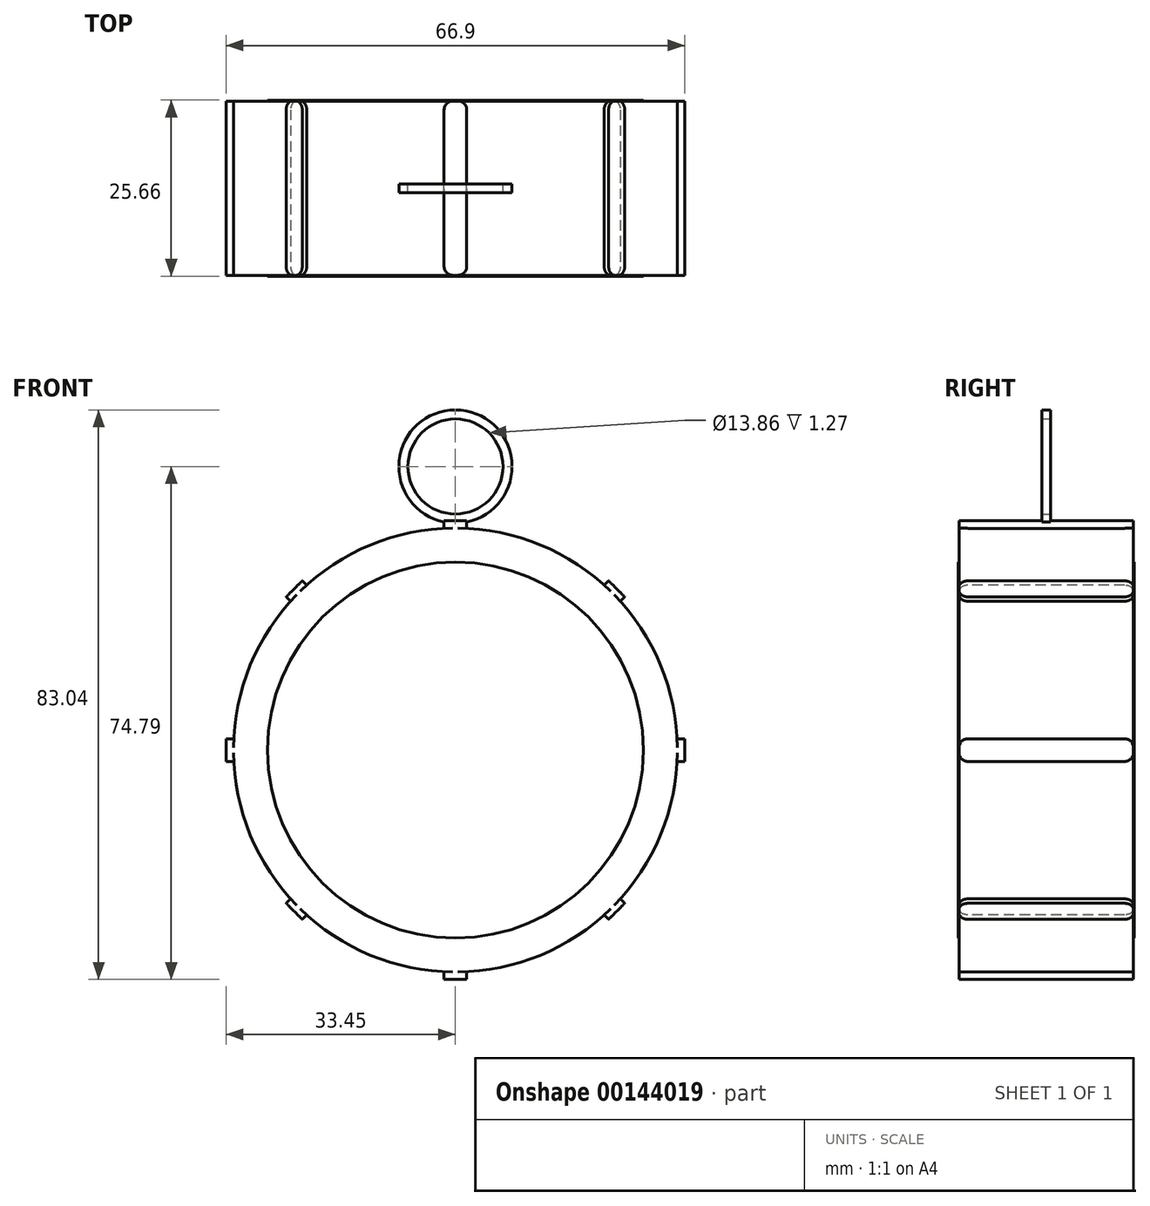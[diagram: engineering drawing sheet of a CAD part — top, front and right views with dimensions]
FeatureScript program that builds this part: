
annotation { "Feature Type Name" : "Feature", "Feature Type Description" : "" }
export const myFeature = defineFeature(function(context is Context, id is Id, definition is map)
    precondition{}
    {
        {
            var Q0;
            Q0=qCreatedBy(makeId("Front.planeOp"),FACE);
            var sketch = newSketch(context, id + "F0", { "sketchPlane" : qUnion([Q0])});
            skCircle(sketch, "E0", {"center": v(0, 0) * mm, "radius": 32.37 * mm});
            skSolve(sketch);
        }
        {
            var Q0;
            Q0 = qSketchRegion(id + "F0", true);
            extrude(context, id + "F1", {"entities" : qUnion([Q0]), "depth" : 25.4 * mm, "symmetric" : true});
        }
        {
            var Q0;
            Q0=qCreatedBy(makeId("Front.planeOp"),FACE);
            var sketch = newSketch(context, id + "F2", { "sketchPlane" : qUnion([Q0])});
            skCircle(sketch, "E1", {"center": v(0, 0) * mm, "radius": 27.4 * mm});
            skSolve(sketch);
        }
        {
            var Q0;
            Q0 = qSketchRegion(id + "F2", true);
            extrude(context, id + "F3", {"entities" : qUnion([Q0]), "operationType" : NewBodyOperationType.ADD, "depth" : 25.65 * mm, "symmetric" : true});
        }
        {
            var Q0;
            Q0=makeQuery(id+"F1.opExtrude","CAP_FACE",FACE,{"disambiguationData":[OSD([sQuery(id+"F0.wireOp",EDGE,"E0")])],"isStart":false});
            var sketch = newSketch(context, id + "F4", { "sketchPlane" : qUnion([Q0])});
            skPoint(sketch, "E2.middle", {"position": v(0, 0) * mm});
            skLineSegment(sketch, "E3", {"start": v(23.5, 23.5) * mm, "end": v(22.34, 24.68) * mm});
            skLineSegment(sketch, "E4", {"start": v(22.34, 24.68) * mm, "end": v(21.7, 24.03) * mm});
            skLineSegment(sketch, "E5", {"start": v(23.5, 23.5) * mm, "end": v(24.68, 22.34) * mm});
            skLineSegment(sketch, "E6", {"start": v(24.68, 22.34) * mm, "end": v(24.03, 21.7) * mm});
            skLineSegment(sketch, "E7.MirrorCS", {"start": v(24.68, -22.34) * mm, "end": v(24.03, -21.7) * mm});
            skLineSegment(sketch, "E8.MirrorCS", {"start": v(23.5, -23.5) * mm, "end": v(24.68, -22.34) * mm});
            skLineSegment(sketch, "E9.MirrorCS", {"start": v(23.5, -23.5) * mm, "end": v(22.34, -24.68) * mm});
            skLineSegment(sketch, "E10.MirrorCS", {"start": v(22.34, -24.68) * mm, "end": v(21.7, -24.03) * mm});
            skLineSegment(sketch, "E11.MirrorCS", {"start": v(-22.34, 24.68) * mm, "end": v(-21.7, 24.03) * mm});
            skLineSegment(sketch, "E12.MirrorCS", {"start": v(-23.5, 23.5) * mm, "end": v(-22.34, 24.68) * mm});
            skLineSegment(sketch, "E13.MirrorCS", {"start": v(-23.5, 23.5) * mm, "end": v(-24.68, 22.34) * mm});
            skLineSegment(sketch, "E14.MirrorCS", {"start": v(-24.68, 22.34) * mm, "end": v(-24.03, 21.7) * mm});
            skLineSegment(sketch, "E15.MirrorCS", {"start": v(-23.5, -23.5) * mm, "end": v(-24.68, -22.34) * mm});
            skLineSegment(sketch, "E16.MirrorCS", {"start": v(-24.68, -22.34) * mm, "end": v(-24.03, -21.7) * mm});
            skLineSegment(sketch, "E17.MirrorCS", {"start": v(-23.5, -23.5) * mm, "end": v(-22.34, -24.68) * mm});
            skLineSegment(sketch, "E18.MirrorCS", {"start": v(-22.34, -24.68) * mm, "end": v(-21.7, -24.03) * mm});
            skLineSegment(sketch, "E19", {"start": v(0, 33.45) * mm, "end": v(-1.65, 33.45) * mm});
            skLineSegment(sketch, "E20", {"start": v(-1.65, 33.45) * mm, "end": v(-1.65, 32.33) * mm});
            skLineSegment(sketch, "E21", {"start": v(0, 33.45) * mm, "end": v(1.65, 33.45) * mm});
            skLineSegment(sketch, "E22", {"start": v(1.65, 33.45) * mm, "end": v(1.65, 32.33) * mm});
            skLineSegment(sketch, "E23.MirrorCS", {"start": v(0, -33.45) * mm, "end": v(-1.65, -33.45) * mm});
            skLineSegment(sketch, "E24.MirrorCS", {"start": v(-1.65, -33.45) * mm, "end": v(-1.65, -32.33) * mm});
            skLineSegment(sketch, "E25.MirrorCS", {"start": v(0, -33.45) * mm, "end": v(1.65, -33.45) * mm});
            skLineSegment(sketch, "E26.MirrorCS", {"start": v(1.65, -33.45) * mm, "end": v(1.65, -32.33) * mm});
            skLineSegment(sketch, "E27", {"start": v(-33.45, 0) * mm, "end": v(-33.45, 1.65) * mm});
            skLineSegment(sketch, "E28", {"start": v(-33.45, 1.65) * mm, "end": v(-32.33, 1.65) * mm});
            skLineSegment(sketch, "E29", {"start": v(-33.45, 0) * mm, "end": v(-33.45, -1.65) * mm});
            skLineSegment(sketch, "E30", {"start": v(-33.45, -1.65) * mm, "end": v(-32.33, -1.65) * mm});
            skLineSegment(sketch, "E31.MirrorCS", {"start": v(33.45, 1.65) * mm, "end": v(32.33, 1.65) * mm});
            skLineSegment(sketch, "E32.MirrorCS", {"start": v(33.45, 0) * mm, "end": v(33.45, 1.65) * mm});
            skLineSegment(sketch, "E33.MirrorCS", {"start": v(33.45, 0) * mm, "end": v(33.45, -1.65) * mm});
            skLineSegment(sketch, "E34.MirrorCS", {"start": v(33.45, -1.65) * mm, "end": v(32.33, -1.65) * mm});
            skSolve(sketch);
        }
        {
            var Q0;
            {var subQ1=sQuery(id+"F4.wireOp",EDGE,"E11.MirrorCS");Q0=makeQuery(id+"F4.imprint","IMPRINT",FACE,{"disambiguationData":[TD([[makeQuery(id+"F4.imprint","IMPRINT",EDGE,{"derivedFrom":subQ1}),-1.0]])]});}
            var Q1;
            Q1=makeQuery(id+"F4.imprint","IMPRINT",FACE,{"disambiguationData":[TD([[makeQuery(id+"F4.imprint","IMPRINT",EDGE,{"derivedFrom":sQuery(id+"F4.wireOp",EDGE,"E3")}),1.0]])]});
            var Q2;
            {var subQ1=sQuery(id+"F4.wireOp",EDGE,"E7.MirrorCS");Q2=makeQuery(id+"F4.imprint","IMPRINT",FACE,{"disambiguationData":[TD([[makeQuery(id+"F4.imprint","IMPRINT",EDGE,{"derivedFrom":subQ1}),1.0]])]});}
            var Q3;
            Q3=makeQuery(id+"F4.imprint","IMPRINT",FACE,{"disambiguationData":[TD([[makeQuery(id+"F4.imprint","IMPRINT",EDGE,{"derivedFrom":sQuery(id+"F4.wireOp",EDGE,"E15.MirrorCS")}),-1.0]])]});
            var Q4;
            Q4=makeQuery(id+"F4.imprint","IMPRINT",FACE,{"disambiguationData":[TD([[makeQuery(id+"F4.imprint","IMPRINT",EDGE,{"derivedFrom":sQuery(id+"F4.wireOp",EDGE,"E23.MirrorCS")}),-1.0]])]});
            var Q5;
            Q5=makeQuery(id+"F4.imprint","IMPRINT",FACE,{"disambiguationData":[TD([[makeQuery(id+"F4.imprint","IMPRINT",EDGE,{"derivedFrom":sQuery(id+"F4.wireOp",EDGE,"E27")}),-1.0]])]});
            var Q6;
            {var subQ1=sQuery(id+"F4.wireOp",EDGE,"E31.MirrorCS");Q6=makeQuery(id+"F4.imprint","IMPRINT",FACE,{"disambiguationData":[TD([[makeQuery(id+"F4.imprint","IMPRINT",EDGE,{"derivedFrom":subQ1}),1.0]])]});}
            var Q7;
            Q7=makeQuery(id+"F4.imprint","IMPRINT",FACE,{"disambiguationData":[TD([[makeQuery(id+"F4.imprint","IMPRINT",EDGE,{"derivedFrom":sQuery(id+"F4.wireOp",EDGE,"E19")}),1.0]])]});
            extrude(context, id + "F5", {"entities" : qUnion([Q0, Q1, Q2, Q3, Q4, Q5, Q6, Q7]), "operationType" : NewBodyOperationType.ADD, "oppositeDirection" : true, "depth" : 25.4 * mm});
        }
        {
            var Q0;
            Q0=makeQuery(id+"Fw6DQcA7fibf5eo_1.opExtrude","SWEPT_EDGE",EDGE,{"disambiguationData":[OSD([sQuery(id+"FSgP6cTA9YGb6rM_1.wireOp",EDGE,"k7nYMJ6Q-pWd2-LHft-FCDd-KbcVLsTTeNov.top"),sQuery(id+"FSgP6cTA9YGb6rM_1.wireOp",EDGE,"k7nYMJ6Q-pWd2-LHft-FCDd-KbcVLsTTeNov.left")])]});
            var Q1;
            Q1=makeQuery(id+"Fw6DQcA7fibf5eo_1.opExtrude","SWEPT_EDGE",EDGE,{"disambiguationData":[OSD([sQuery(id+"FSgP6cTA9YGb6rM_1.wireOp",EDGE,"k7nYMJ6Q-pWd2-LHft-FCDd-KbcVLsTTeNov.bottom"),sQuery(id+"FSgP6cTA9YGb6rM_1.wireOp",EDGE,"k7nYMJ6Q-pWd2-LHft-FCDd-KbcVLsTTeNov.left")])]});
            var Q2;
            Q2=makeQuery(id+"Fw6DQcA7fibf5eo_1.opExtrude","SWEPT_EDGE",EDGE,{"disambiguationData":[OSD([sQuery(id+"FSgP6cTA9YGb6rM_1.wireOp",EDGE,"k7nYMJ6Q-pWd2-LHft-FCDd-KbcVLsTTeNov.top"),sQuery(id+"FSgP6cTA9YGb6rM_1.wireOp",EDGE,"k7nYMJ6Q-pWd2-LHft-FCDd-KbcVLsTTeNov.right")])]});
            var Q3;
            Q3=makeQuery(id+"Fw6DQcA7fibf5eo_1.opExtrude","SWEPT_EDGE",EDGE,{"disambiguationData":[OSD([sQuery(id+"FSgP6cTA9YGb6rM_1.wireOp",EDGE,"k7nYMJ6Q-pWd2-LHft-FCDd-KbcVLsTTeNov.bottom"),sQuery(id+"FSgP6cTA9YGb6rM_1.wireOp",EDGE,"k7nYMJ6Q-pWd2-LHft-FCDd-KbcVLsTTeNov.right")])]});
            var Q4;
            Q4=makeQuery(id+"F5.opExtrude","CAP_EDGE",EDGE,{"disambiguationData":[OSD([sQuery(id+"F4.wireOp",EDGE,"E7.MirrorCS")])],"isStart":false});
            var Q5;
            Q5=makeQuery(id+"F5.opExtrude","CAP_EDGE",EDGE,{"disambiguationData":[OSD([sQuery(id+"F4.wireOp",EDGE,"E10.MirrorCS")])],"isStart":false});
            var Q6;
            Q6=makeQuery(id+"F5.opExtrude","CAP_EDGE",EDGE,{"disambiguationData":[OSD([sQuery(id+"F4.wireOp",EDGE,"E7.MirrorCS")])],"isStart":true});
            var Q7;
            Q7=makeQuery(id+"F5.opExtrude","CAP_EDGE",EDGE,{"disambiguationData":[OSD([sQuery(id+"F4.wireOp",EDGE,"E10.MirrorCS")])],"isStart":true});
            var Q8;
            Q8=makeQuery(id+"F5.opExtrude","CAP_EDGE",EDGE,{"disambiguationData":[OSD([sQuery(id+"F4.wireOp",EDGE,"E6")])],"isStart":true});
            var Q9;
            Q9=makeQuery(id+"F5.opExtrude","CAP_EDGE",EDGE,{"disambiguationData":[OSD([sQuery(id+"F4.wireOp",EDGE,"E4")])],"isStart":true});
            var Q10;
            Q10=makeQuery(id+"F5.opExtrude","CAP_EDGE",EDGE,{"disambiguationData":[OSD([sQuery(id+"F4.wireOp",EDGE,"E4")])],"isStart":false});
            var Q11;
            Q11=makeQuery(id+"F5.opExtrude","CAP_EDGE",EDGE,{"disambiguationData":[OSD([sQuery(id+"F4.wireOp",EDGE,"E6")])],"isStart":false});
            var Q12;
            Q12=makeQuery(id+"F361BySn9YO4Jxk_1.opExtrude","SWEPT_EDGE",EDGE,{"disambiguationData":[OSD([sQuery(id+"FlEHG8BH6hBnB3Y_1.wireOp",EDGE,"KlyghsjG-MX3N-1A5D-2EYQ-8ZTh4fC2w1Wf.top"),sQuery(id+"FlEHG8BH6hBnB3Y_1.wireOp",EDGE,"KlyghsjG-MX3N-1A5D-2EYQ-8ZTh4fC2w1Wf.left")])]});
            var Q13;
            Q13=makeQuery(id+"F361BySn9YO4Jxk_1.opExtrude","SWEPT_EDGE",EDGE,{"disambiguationData":[OSD([sQuery(id+"FlEHG8BH6hBnB3Y_1.wireOp",EDGE,"KlyghsjG-MX3N-1A5D-2EYQ-8ZTh4fC2w1Wf.top"),sQuery(id+"FlEHG8BH6hBnB3Y_1.wireOp",EDGE,"KlyghsjG-MX3N-1A5D-2EYQ-8ZTh4fC2w1Wf.right")])]});
            var Q14;
            Q14=makeQuery(id+"F5.opExtrude","CAP_EDGE",EDGE,{"disambiguationData":[OSD([sQuery(id+"F4.wireOp",EDGE,"E11.MirrorCS")])],"isStart":false});
            var Q15;
            Q15=makeQuery(id+"F5.opExtrude","CAP_EDGE",EDGE,{"disambiguationData":[OSD([sQuery(id+"F4.wireOp",EDGE,"E14.MirrorCS")])],"isStart":false});
            var Q16;
            Q16=makeQuery(id+"FvUOm0vH0djjMBF_1.opExtrude","SWEPT_EDGE",EDGE,{"disambiguationData":[OSD([sQuery(id+"F7Q19J1wl6F7tsK_1.wireOp",EDGE,"RNEpTE1L-NMeB-yVCJ-Lo0h-tUHyB7hWAidC.top"),sQuery(id+"F7Q19J1wl6F7tsK_1.wireOp",EDGE,"RNEpTE1L-NMeB-yVCJ-Lo0h-tUHyB7hWAidC.right")])]});
            var Q17;
            Q17=makeQuery(id+"FvUOm0vH0djjMBF_1.opExtrude","SWEPT_EDGE",EDGE,{"disambiguationData":[OSD([sQuery(id+"F7Q19J1wl6F7tsK_1.wireOp",EDGE,"RNEpTE1L-NMeB-yVCJ-Lo0h-tUHyB7hWAidC.bottom"),sQuery(id+"F7Q19J1wl6F7tsK_1.wireOp",EDGE,"RNEpTE1L-NMeB-yVCJ-Lo0h-tUHyB7hWAidC.right")])]});
            var Q18;
            Q18=makeQuery(id+"F5.opExtrude","CAP_EDGE",EDGE,{"disambiguationData":[OSD([sQuery(id+"F4.wireOp",EDGE,"E16.MirrorCS")])],"isStart":false});
            var Q19;
            Q19=makeQuery(id+"F5.opExtrude","CAP_EDGE",EDGE,{"disambiguationData":[OSD([sQuery(id+"F4.wireOp",EDGE,"E18.MirrorCS")])],"isStart":false});
            var Q20;
            Q20=makeQuery(id+"FQhpxXkMpCYbe5R_1.opExtrude","SWEPT_EDGE",EDGE,{"disambiguationData":[OSD([sQuery(id+"FJzGD1dESdxRgwG_1.wireOp",EDGE,"Jid228Rw-LOJq-qx2D-1DFM-3pvaorZhpX5U.bottom"),sQuery(id+"FJzGD1dESdxRgwG_1.wireOp",EDGE,"Jid228Rw-LOJq-qx2D-1DFM-3pvaorZhpX5U.right")])]});
            var Q21;
            Q21=makeQuery(id+"FQhpxXkMpCYbe5R_1.opExtrude","SWEPT_EDGE",EDGE,{"disambiguationData":[OSD([sQuery(id+"FJzGD1dESdxRgwG_1.wireOp",EDGE,"Jid228Rw-LOJq-qx2D-1DFM-3pvaorZhpX5U.bottom"),sQuery(id+"FJzGD1dESdxRgwG_1.wireOp",EDGE,"Jid228Rw-LOJq-qx2D-1DFM-3pvaorZhpX5U.left")])]});
            var Q22;
            Q22=makeQuery(id+"FQhpxXkMpCYbe5R_1.opExtrude","SWEPT_EDGE",EDGE,{"disambiguationData":[OSD([sQuery(id+"FJzGD1dESdxRgwG_1.wireOp",EDGE,"Jid228Rw-LOJq-qx2D-1DFM-3pvaorZhpX5U.top"),sQuery(id+"FJzGD1dESdxRgwG_1.wireOp",EDGE,"Jid228Rw-LOJq-qx2D-1DFM-3pvaorZhpX5U.right")])]});
            var Q23;
            Q23=makeQuery(id+"FQhpxXkMpCYbe5R_1.opExtrude","SWEPT_EDGE",EDGE,{"disambiguationData":[OSD([sQuery(id+"FJzGD1dESdxRgwG_1.wireOp",EDGE,"Jid228Rw-LOJq-qx2D-1DFM-3pvaorZhpX5U.top"),sQuery(id+"FJzGD1dESdxRgwG_1.wireOp",EDGE,"Jid228Rw-LOJq-qx2D-1DFM-3pvaorZhpX5U.left")])]});
            var Q24;
            Q24=makeQuery(id+"F5.opExtrude","CAP_EDGE",EDGE,{"disambiguationData":[OSD([sQuery(id+"F4.wireOp",EDGE,"E18.MirrorCS")])],"isStart":true});
            var Q25;
            Q25=makeQuery(id+"F5.opExtrude","CAP_EDGE",EDGE,{"disambiguationData":[OSD([sQuery(id+"F4.wireOp",EDGE,"E16.MirrorCS")])],"isStart":true});
            var Q26;
            Q26=makeQuery(id+"FvUOm0vH0djjMBF_1.opExtrude","SWEPT_EDGE",EDGE,{"disambiguationData":[OSD([sQuery(id+"F7Q19J1wl6F7tsK_1.wireOp",EDGE,"RNEpTE1L-NMeB-yVCJ-Lo0h-tUHyB7hWAidC.bottom"),sQuery(id+"F7Q19J1wl6F7tsK_1.wireOp",EDGE,"RNEpTE1L-NMeB-yVCJ-Lo0h-tUHyB7hWAidC.left")])]});
            var Q27;
            Q27=makeQuery(id+"FvUOm0vH0djjMBF_1.opExtrude","SWEPT_EDGE",EDGE,{"disambiguationData":[OSD([sQuery(id+"F7Q19J1wl6F7tsK_1.wireOp",EDGE,"RNEpTE1L-NMeB-yVCJ-Lo0h-tUHyB7hWAidC.top"),sQuery(id+"F7Q19J1wl6F7tsK_1.wireOp",EDGE,"RNEpTE1L-NMeB-yVCJ-Lo0h-tUHyB7hWAidC.left")])]});
            var Q28;
            Q28=makeQuery(id+"F5.opExtrude","CAP_EDGE",EDGE,{"disambiguationData":[OSD([sQuery(id+"F4.wireOp",EDGE,"E14.MirrorCS")])],"isStart":true});
            var Q29;
            Q29=makeQuery(id+"F5.opExtrude","CAP_EDGE",EDGE,{"disambiguationData":[OSD([sQuery(id+"F4.wireOp",EDGE,"E11.MirrorCS")])],"isStart":true});
            var Q30;
            Q30=makeQuery(id+"F361BySn9YO4Jxk_1.opExtrude","SWEPT_EDGE",EDGE,{"disambiguationData":[OSD([sQuery(id+"FlEHG8BH6hBnB3Y_1.wireOp",EDGE,"KlyghsjG-MX3N-1A5D-2EYQ-8ZTh4fC2w1Wf.bottom"),sQuery(id+"FlEHG8BH6hBnB3Y_1.wireOp",EDGE,"KlyghsjG-MX3N-1A5D-2EYQ-8ZTh4fC2w1Wf.right")])]});
            var Q31;
            Q31=makeQuery(id+"F361BySn9YO4Jxk_1.opExtrude","SWEPT_EDGE",EDGE,{"disambiguationData":[OSD([sQuery(id+"FlEHG8BH6hBnB3Y_1.wireOp",EDGE,"KlyghsjG-MX3N-1A5D-2EYQ-8ZTh4fC2w1Wf.bottom"),sQuery(id+"FlEHG8BH6hBnB3Y_1.wireOp",EDGE,"KlyghsjG-MX3N-1A5D-2EYQ-8ZTh4fC2w1Wf.left")])]});
            fillet(context, id + "F6", {"entities" : qUnion([Q0, Q1, Q2, Q3, Q4, Q5, Q6, Q7, Q8, Q9, Q10, Q11, Q12, Q13, Q14, Q15, Q16, Q17, Q18, Q19, Q20, Q21, Q22, Q23, Q24, Q25, Q26, Q27, Q28, Q29, Q30, Q31]), "radius" : 1.27 * mm, "tangentPropagation" : true, "allowEdgeOverflow" : false});
        }
        {
            var Q0;
            Q0=makeQuery(id+"F5.opExtrude","CAP_EDGE",EDGE,{"disambiguationData":[OSD([sQuery(id+"F4.wireOp",EDGE,"E20")])],"isStart":false});
            var Q1;
            Q1=makeQuery(id+"F5.opExtrude","CAP_EDGE",EDGE,{"disambiguationData":[OSD([sQuery(id+"F4.wireOp",EDGE,"E22")])],"isStart":false});
            var Q2;
            Q2=makeQuery(id+"F5.opExtrude","CAP_EDGE",EDGE,{"disambiguationData":[OSD([sQuery(id+"F4.wireOp",EDGE,"E20")])],"isStart":true});
            var Q3;
            Q3=makeQuery(id+"F5.opExtrude","CAP_EDGE",EDGE,{"disambiguationData":[OSD([sQuery(id+"F4.wireOp",EDGE,"E22")])],"isStart":true});
            var Q4;
            Q4=makeQuery(id+"F5.opExtrude","CAP_EDGE",EDGE,{"disambiguationData":[OSD([sQuery(id+"F4.wireOp",EDGE,"E30")])],"isStart":false});
            var Q5;
            Q5=makeQuery(id+"F5.opExtrude","CAP_EDGE",EDGE,{"disambiguationData":[OSD([sQuery(id+"F4.wireOp",EDGE,"E28")])],"isStart":true});
            var Q6;
            Q6=makeQuery(id+"F5.opExtrude","CAP_EDGE",EDGE,{"disambiguationData":[OSD([sQuery(id+"F4.wireOp",EDGE,"E30")])],"isStart":true});
            var Q7;
            Q7=makeQuery(id+"F5.opExtrude","CAP_EDGE",EDGE,{"disambiguationData":[OSD([sQuery(id+"F4.wireOp",EDGE,"E28")])],"isStart":false});
            var Q8;
            Q8=makeQuery(id+"F5.opExtrude","CAP_EDGE",EDGE,{"disambiguationData":[OSD([sQuery(id+"F4.wireOp",EDGE,"E24.MirrorCS")])],"isStart":false});
            var Q9;
            Q9=makeQuery(id+"F5.opExtrude","CAP_EDGE",EDGE,{"disambiguationData":[OSD([sQuery(id+"F4.wireOp",EDGE,"E26.MirrorCS")])],"isStart":false});
            var Q10;
            Q10=makeQuery(id+"F5.opExtrude","CAP_EDGE",EDGE,{"disambiguationData":[OSD([sQuery(id+"F4.wireOp",EDGE,"E31.MirrorCS")])],"isStart":false});
            var Q11;
            Q11=makeQuery(id+"F5.opExtrude","CAP_EDGE",EDGE,{"disambiguationData":[OSD([sQuery(id+"F4.wireOp",EDGE,"E34.MirrorCS")])],"isStart":false});
            var Q12;
            Q12=makeQuery(id+"F5.opExtrude","CAP_EDGE",EDGE,{"disambiguationData":[OSD([sQuery(id+"F4.wireOp",EDGE,"E34.MirrorCS")])],"isStart":true});
            var Q13;
            Q13=makeQuery(id+"F5.opExtrude","CAP_EDGE",EDGE,{"disambiguationData":[OSD([sQuery(id+"F4.wireOp",EDGE,"E31.MirrorCS")])],"isStart":true});
            var Q14;
            Q14=makeQuery(id+"F5.opExtrude","CAP_EDGE",EDGE,{"disambiguationData":[OSD([sQuery(id+"F4.wireOp",EDGE,"E26.MirrorCS")])],"isStart":true});
            var Q15;
            Q15=makeQuery(id+"F5.opExtrude","CAP_EDGE",EDGE,{"disambiguationData":[OSD([sQuery(id+"F4.wireOp",EDGE,"E24.MirrorCS")])],"isStart":true});
            fillet(context, id + "F7", {"entities" : qUnion([Q0, Q1, Q2, Q3, Q4, Q5, Q6, Q7, Q8, Q9, Q10, Q11, Q12, Q13, Q14, Q15]), "radius" : 1.27 * mm, "tangentPropagation" : true, "allowEdgeOverflow" : false});
        }
        {
            var Q0;
            Q0=qCreatedBy(makeId("Front.planeOp"),FACE);
            var sketch = newSketch(context, id + "F8", { "sketchPlane" : qUnion([Q0])});
            skCircle(sketch, "E35", {"center": v(0, 41.34) * mm, "radius": 8.25 * mm});
            skCircle(sketch, "E36", {"center": v(0, 41.34) * mm, "radius": 6.93 * mm});
            skSolve(sketch);
        }
        {
            var Q0;
            Q0 = qSketchRegion(id + "F8", true);
            extrude(context, id + "F9", {"entities" : qUnion([Q0]), "operationType" : NewBodyOperationType.ADD, "depth" : 1.27 * mm, "symmetric" : true});
        }
    });
